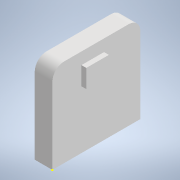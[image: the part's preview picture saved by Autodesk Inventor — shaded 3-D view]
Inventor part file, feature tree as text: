
AUTODESK INVENTOR PART (.ipt)
format: ipt  version: 2022 (Build 260153000, 153)  size: 105,472 bytes
history: native  units: in
note: dims shown in document units (in); Inventor stores cm internally (conversion verified against a paired STEP export)
features: sketch x3, extrude x2, fillet x1
ambient origin geometry x8: Origin, YZ Plane, XZ Plane, XY Plane, X Axis, Y Axis, Z Axis, Center Point
bodies: Solid1 (feature_tree)
feature tree (6):
  sketch  "Sketch1"  dims[d0=3.6in d1=18.0in d2=18.0in d3=0.0in]
  extrude  "Extrusion1"  Depth=18.0in
  fillet  "Fillet1"  Radius=18.0in
  extrude  "Extrusion2"  Depth=1.0in TaperAngle=0.0deg
  sketch  "Sketch2"  dims[d4=2.4in d5=1.0in d6=0.0in]
  sketch  "Sketch3"
